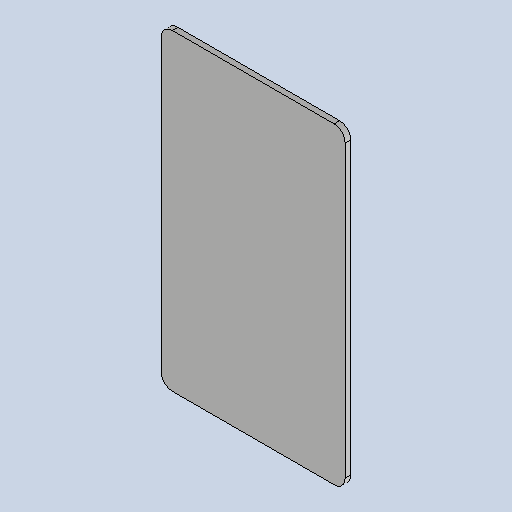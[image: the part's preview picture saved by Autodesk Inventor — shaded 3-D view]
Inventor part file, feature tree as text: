
AUTODESK INVENTOR PART (.ipt)
format: ipt  version: 2025 (Build 290162010, 162A)  size: 143,872 bytes
history: native  units: mm
features: sheet_metal_op x1, chamfer x1, sketch x1, other x1
ambient origin geometry x8: Origin, YZ Plane, XZ Plane, XY Plane, X Axis, Y Axis, Z Axis, Center Point
bodies: Solid1 (feature_tree)
feature tree (4):
  sheet_metal_op  "Face1"
  chamfer  "Corner Round1"
  sketch  "Sketch1"  dims[d0=100.0mm d1=170.0mm d2=3.0mm d3=6.0mm]
  other  "Plate1"
